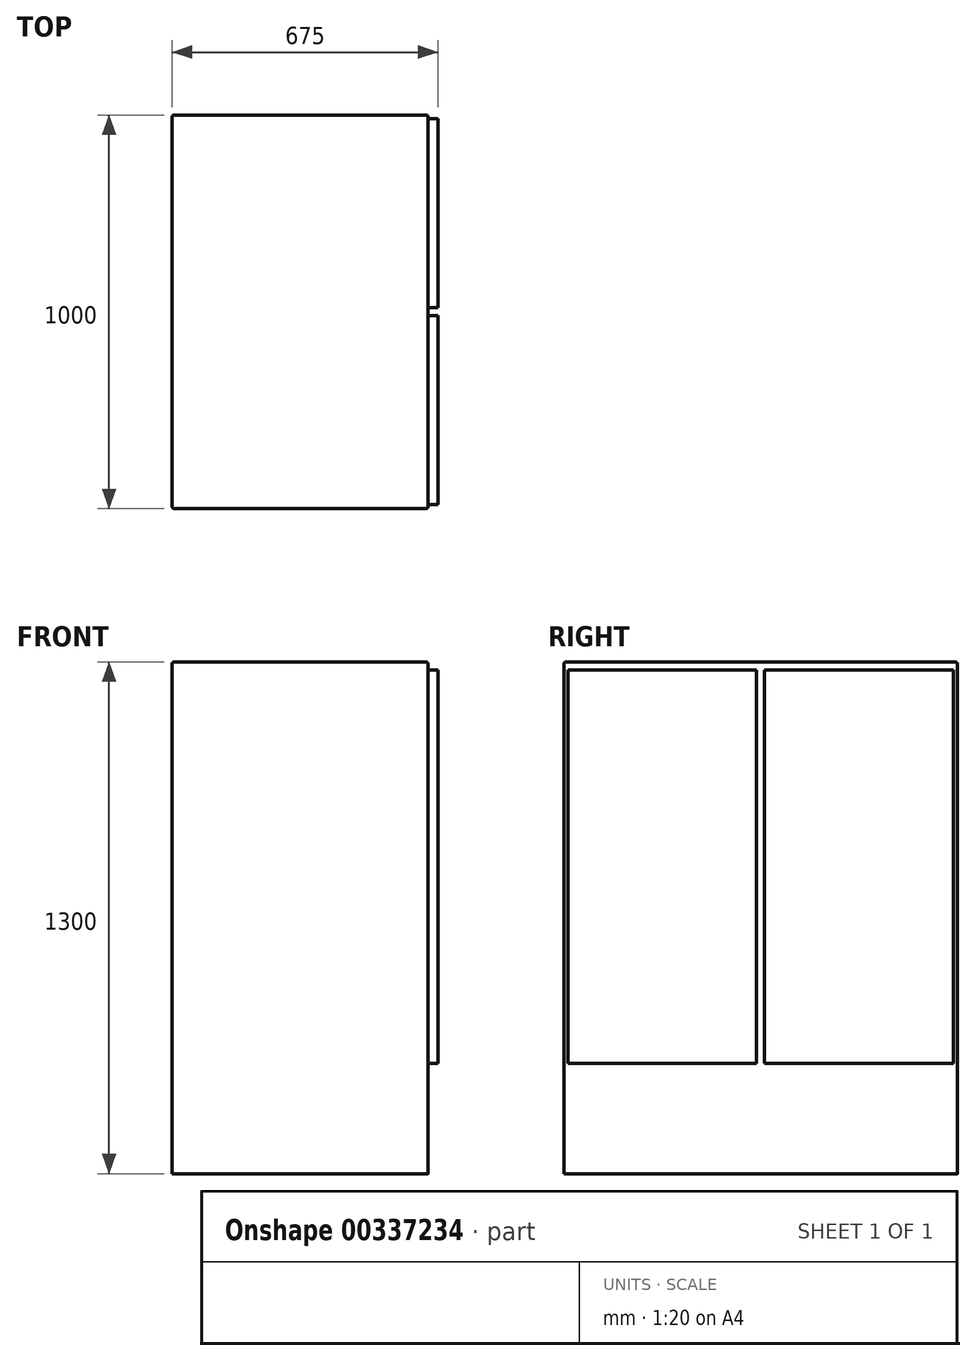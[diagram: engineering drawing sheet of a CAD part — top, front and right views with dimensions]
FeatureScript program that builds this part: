
annotation { "Feature Type Name" : "Feature", "Feature Type Description" : "" }
export const myFeature = defineFeature(function(context is Context, id is Id, definition is map)
    precondition{}
    {
        {
            var Q0;
            Q0=qCreatedBy(makeId("Front.planeOp"),FACE);
            var sketch = newSketch(context, id + "F0", { "sketchPlane" : qUnion([Q0])});
            skLineSegment(sketch, "E0.bottom", {"start": v(0, 0) * mm, "end": v(650, 0) * mm});
            skLineSegment(sketch, "E0.top", {"start": v(0, 1300) * mm, "end": v(650, 1300) * mm});
            skLineSegment(sketch, "E0.left", {"start": v(0, 0) * mm, "end": v(0, 1300) * mm});
            skLineSegment(sketch, "E0.right", {"start": v(650, 0) * mm, "end": v(650, 1300) * mm});
            skSolve(sketch);
        }
        {
            var Q0;
            Q0=makeQuery(id+"F0.imprint","IMPRINT",FACE,{"disambiguationData":[TD([[makeQuery(id+"F0.imprint","IMPRINT",EDGE,{"derivedFrom":sQuery(id+"F0.wireOp",EDGE,"E0.bottom")}),1.0]])]});
            extrude(context, id + "F1", {"entities" : qUnion([Q0]), "depth" : 1000 * mm});
        }
        {
            var Q0;
            Q0=makeQuery(id+"F1.opExtrude","SWEPT_FACE",FACE,{"disambiguationData":[OSD([sQuery(id+"F0.wireOp",EDGE,"E0.right")])]});
            var sketch = newSketch(context, id + "F2", { "sketchPlane" : qUnion([Q0])});
            skLineSegment(sketch, "E1.top", {"start": v(-990, 280) * mm, "end": v(-510, 280) * mm});
            skLineSegment(sketch, "E1.left", {"start": v(-990, 1280) * mm, "end": v(-990, 280) * mm});
            skLineSegment(sketch, "E1.right", {"start": v(-510, 1280) * mm, "end": v(-510, 280) * mm});
            skLineSegment(sketch, "E2.top", {"start": v(-10, 280) * mm, "end": v(-490, 280) * mm});
            skLineSegment(sketch, "E2.left", {"start": v(-10, 1280) * mm, "end": v(-10, 280) * mm});
            skLineSegment(sketch, "E2.right", {"start": v(-490, 1280) * mm, "end": v(-490, 280) * mm});
            skLineSegment(sketch, "E3", {"start": v(-500, 1300) * mm, "end": v(-500, 0) * mm});
            skLineSegment(sketch, "E4", {"start": v(-990, 1280) * mm, "end": v(-510, 1280) * mm});
            skLineSegment(sketch, "E5", {"start": v(-490, 1280) * mm, "end": v(-10, 1280) * mm});
            skSolve(sketch);
        }
        {
            var Q0;
            Q0=makeQuery(id+"F2.imprint","IMPRINT",FACE,{"disambiguationData":[TD([[makeQuery(id+"F2.imprint","IMPRINT",EDGE,{"derivedFrom":sQuery(id+"F2.wireOp",EDGE,"E2.top")}),-1.0]])]});
            var Q1;
            Q1=makeQuery(id+"F2.imprint","IMPRINT",FACE,{"disambiguationData":[TD([[makeQuery(id+"F2.imprint","IMPRINT",EDGE,{"derivedFrom":sQuery(id+"F2.wireOp",EDGE,"E1.top")}),1.0]])]});
            extrude(context, id + "F3", {"entities" : qUnion([Q0, Q1]), "operationType" : NewBodyOperationType.ADD, "depth" : 25 * mm});
        }
        {
            var Q0;
            Q0=makeQuery(id+"F1.opExtrude","CAP_EDGE",EDGE,{"disambiguationData":[OSD([sQuery(id+"F0.wireOp",EDGE,"E0.top")])],"isStart":false});
            var Q1;
            Q1=makeQuery(id+"F1.opExtrude","CAP_EDGE",EDGE,{"disambiguationData":[OSD([sQuery(id+"F0.wireOp",EDGE,"E0.left")])],"isStart":false});
            var Q2;
            Q2=makeQuery(id+"F1.opExtrude","CAP_EDGE",EDGE,{"disambiguationData":[OSD([sQuery(id+"F0.wireOp",EDGE,"E0.right")])],"isStart":false});
            var Q3;
            Q3=makeQuery(id+"F1.opExtrude","SWEPT_EDGE",EDGE,{"disambiguationData":[OSD([sQuery(id+"F0.wireOp",EDGE,"E0.top"),sQuery(id+"F0.wireOp",EDGE,"E0.right")])]});
            var Q4;
            Q4=makeQuery(id+"F1.opExtrude","SWEPT_EDGE",EDGE,{"disambiguationData":[OSD([sQuery(id+"F0.wireOp",EDGE,"E0.top"),sQuery(id+"F0.wireOp",EDGE,"E0.left")])]});
            var Q5;
            Q5=makeQuery(id+"F1.opExtrude","CAP_EDGE",EDGE,{"disambiguationData":[OSD([sQuery(id+"F0.wireOp",EDGE,"E0.top")])],"isStart":true});
            var Q6;
            Q6=makeQuery(id+"F1.opExtrude","CAP_EDGE",EDGE,{"disambiguationData":[OSD([sQuery(id+"F0.wireOp",EDGE,"E0.right")])],"isStart":true});
            var Q7;
            Q7=makeQuery(id+"F1.opExtrude","CAP_EDGE",EDGE,{"disambiguationData":[OSD([sQuery(id+"F0.wireOp",EDGE,"E0.left")])],"isStart":true});
            fillet(context, id + "F4", {"entities" : qUnion([Q0, Q1, Q2, Q3, Q4, Q5, Q6, Q7]), "radius" : 5 * mm, "tangentPropagation" : true, "allowEdgeOverflow" : false});
        }
    });
